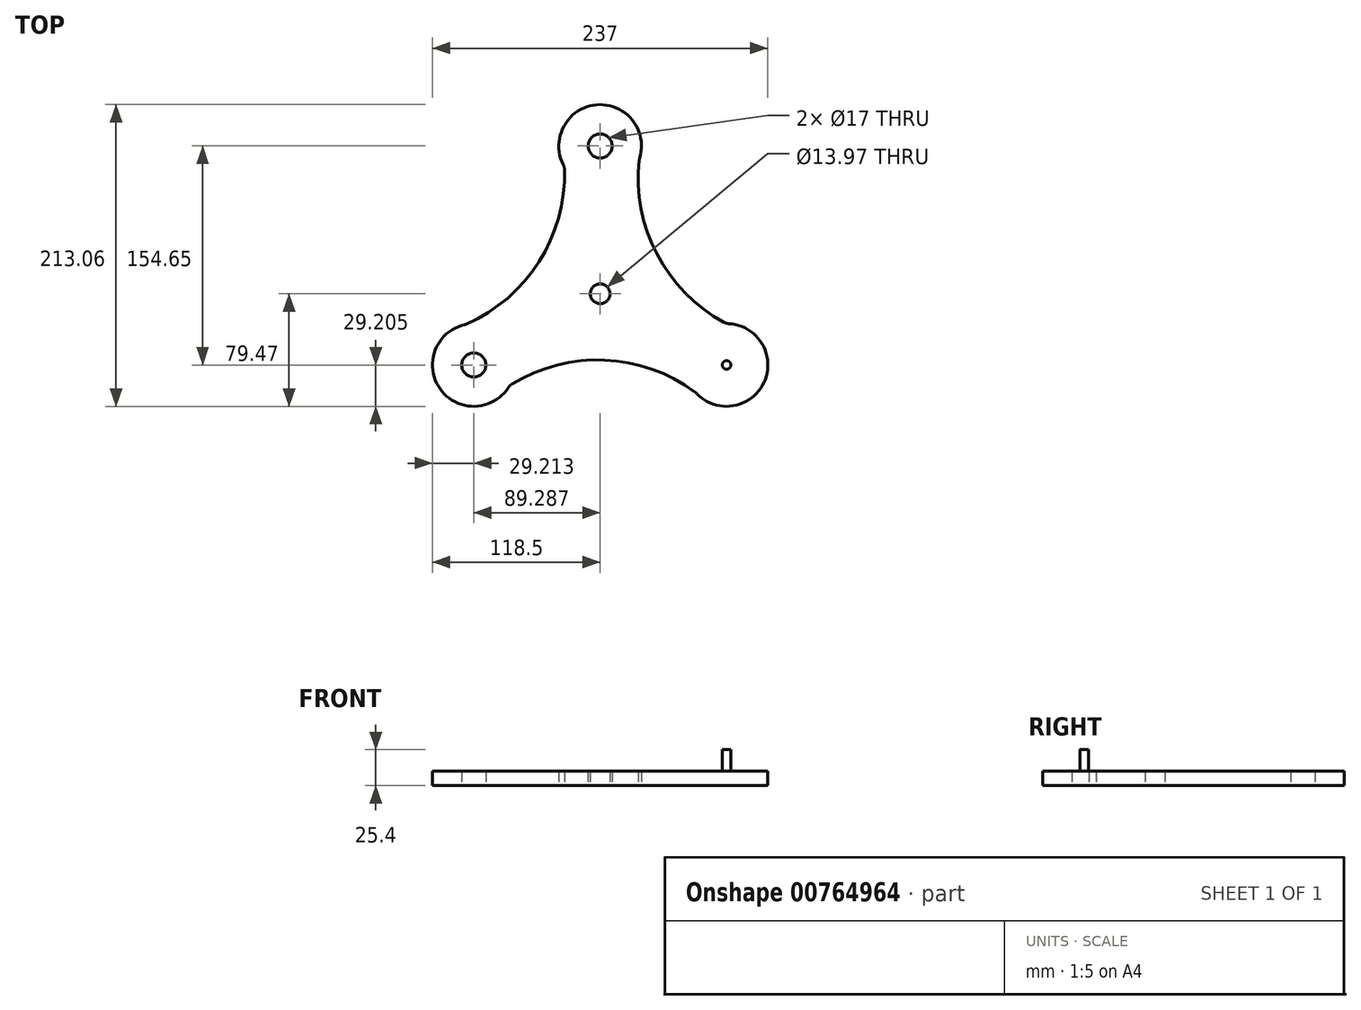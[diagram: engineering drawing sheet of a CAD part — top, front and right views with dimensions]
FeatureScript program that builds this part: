
annotation { "Feature Type Name" : "Feature", "Feature Type Description" : "" }
export const myFeature = defineFeature(function(context is Context, id is Id, definition is map)
    precondition{}
    {
        {
            var Q0;
            Q0=qCreatedBy(makeId("Top.planeOp"),FACE);
            var sketch = newSketch(context, id + "F0", { "sketchPlane" : qUnion([Q0])});
            skCircle(sketch, "E0", {"center": v(0, 0) * mm, "radius": 6.99 * mm});
            skCircle(sketch, "E1", {"center": v(0, 104.39) * mm, "radius": 8.5 * mm});
            skArc(sketch, "E2", {"start": v(27.76, 95.28) * mm, "mid": v(-3.01, 133.44) * mm, "end": v(-25.3, 89.78) * mm});
            skPoint(sketch, "E3.center.orphan", {"position": v(87.86, -42.04) * mm});
            skPoint(sketch, "E4.center.orphan", {"position": v(-75.14, -42.04) * mm});
            skArc(sketch, "E5.1.0", {"start": v(-95.28, -21.68) * mm, "mid": v(-112.94, -67.4) * mm, "end": v(-64, -64.87) * mm});
            skCircle(sketch, "E5.1.1", {"center": v(-89.29, -50.26) * mm, "radius": 8.5 * mm});
            skArc(sketch, "E5.2.0", {"start": v(67.53, -69.75) * mm, "mid": v(115.96, -62.18) * mm, "end": v(89.29, -21.06) * mm});
            skPoint(sketch, "E5.center", {"position": v(0, 1.29) * mm});
            skArc(sketch, "E6", {"start": v(29.2, 104.38) * mm, "mid": v(38.3, 31.63) * mm, "end": v(89.29, -21.06) * mm});
            skArc(sketch, "E7.1.0", {"start": v(-103.9, -24.97) * mm, "mid": v(-45.42, 19.27) * mm, "end": v(-25.3, 89.78) * mm});
            skArc(sketch, "E7.2.0", {"start": v(74.68, -75.56) * mm, "mid": v(7.13, -47.05) * mm, "end": v(-64, -64.87) * mm});
            skCircle(sketch, "E8", {"center": v(89.29, -50.27) * mm, "radius": 3.02 * mm});
            skSolve(sketch);
        }
        {
            var Q0;
            Q0=qSketchRegion(id+"F0",true);
            extrude(context, id + "F1", {"entities" : qUnion([Q0]), "depth" : 10.16 * mm, "offsetDistance" : 25.4 * mm});
        }
        {
            var Q0;
            Q0=makeQuery(id+"F1.opExtrude","SWEPT_EDGE",EDGE,{"disambiguationData":[OSD([sQuery(id+"F0.wireOp",EDGE,"E2"),sQuery(id+"F0.wireOp",EDGE,"E6")])]});
            var Q1;
            Q1=makeQuery(id+"F1.opExtrude","SWEPT_EDGE",EDGE,{"disambiguationData":[OSD([sQuery(id+"F0.wireOp",EDGE,"E2"),sQuery(id+"F0.wireOp",EDGE,"E7.1.0")])]});
            var Q2;
            Q2=makeQuery(id+"F1.opExtrude","SWEPT_EDGE",EDGE,{"disambiguationData":[OSD([sQuery(id+"F0.wireOp",EDGE,"E5.1.0"),sQuery(id+"F0.wireOp",EDGE,"E7.2.0")])]});
            var Q3;
            Q3=makeQuery(id+"F1.opExtrude","SWEPT_EDGE",EDGE,{"disambiguationData":[OSD([sQuery(id+"F0.wireOp",EDGE,"E5.1.0"),sQuery(id+"F0.wireOp",EDGE,"E7.1.0")])]});
            var Q4;
            Q4=makeQuery(id+"F1.opExtrude","SWEPT_EDGE",EDGE,{"disambiguationData":[OSD([sQuery(id+"F0.wireOp",EDGE,"E5.2.0"),sQuery(id+"F0.wireOp",EDGE,"E7.2.0")])]});
            var Q5;
            Q5=makeQuery(id+"F1.opExtrude","SWEPT_EDGE",EDGE,{"disambiguationData":[OSD([sQuery(id+"F0.wireOp",EDGE,"E5.2.0"),sQuery(id+"F0.wireOp",EDGE,"E6")])]});
            fillet(context, id + "F2", {"entities" : qUnion([Q0, Q1, Q2, Q3, Q4, Q5]), "radius" : 7.62 * mm, "tangentPropagation" : true, "allowEdgeOverflow" : false});
        }
        {
            var Q0;
            Q0=makeQuery(id+"F0.imprint","IMPRINT",FACE,{"disambiguationData":[TD([[makeQuery(id+"F0.imprint","IMPRINT",EDGE,{"derivedFrom":sQuery(id+"F0.wireOp",EDGE,"E8")}),1.0]])]});
            extrude(context, id + "F3", {"entities" : qUnion([Q0]), "operationType" : NewBodyOperationType.ADD, "depth" : 25.4 * mm, "offsetDistance" : 25.4 * mm});
        }
    });
